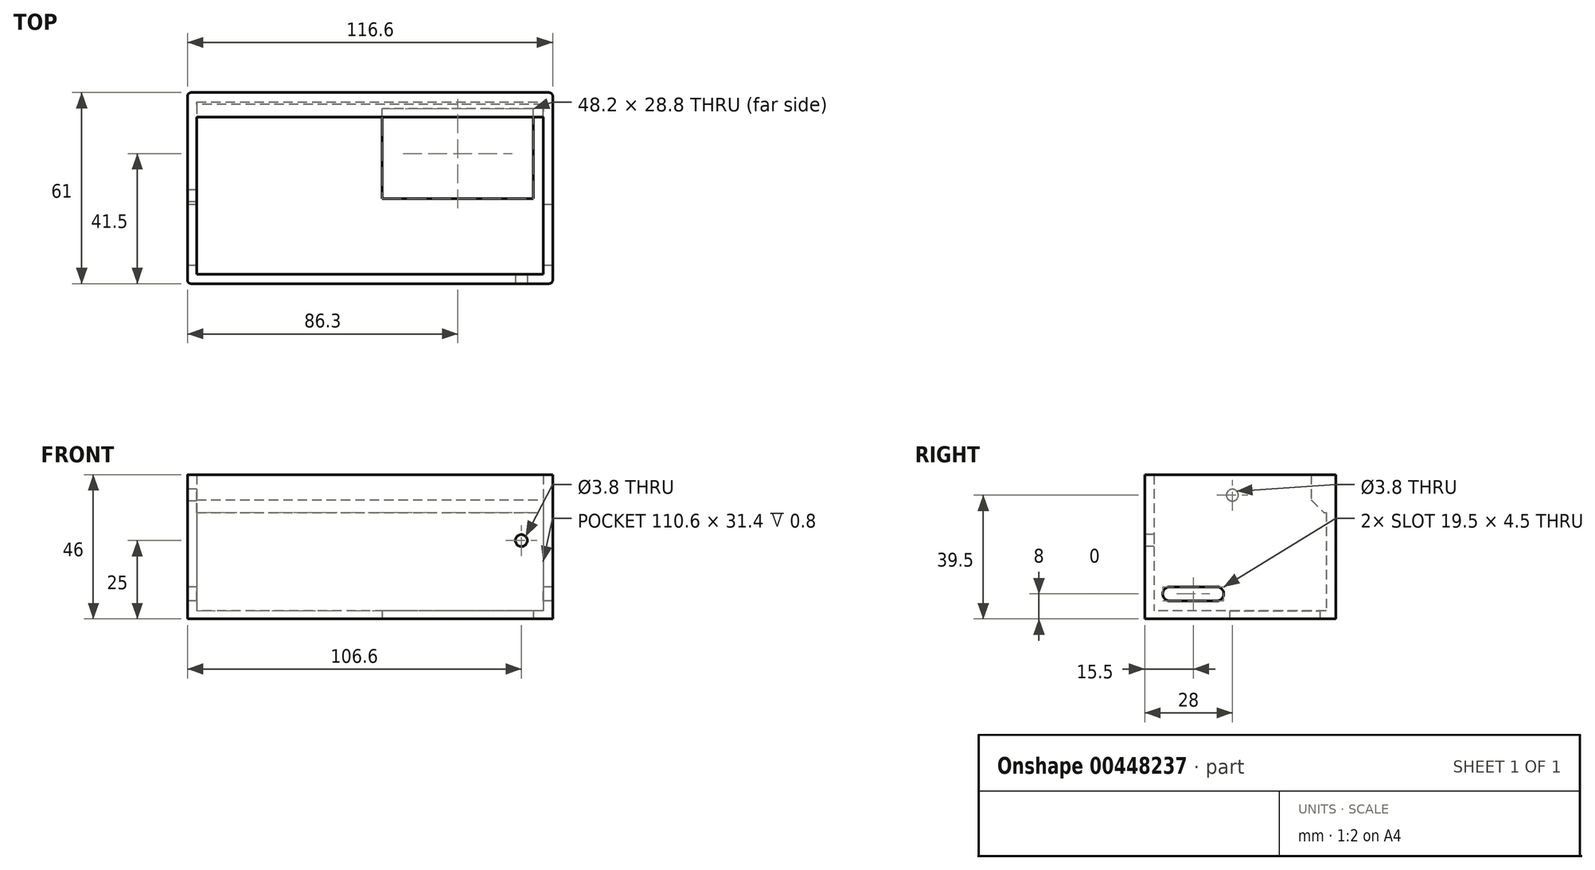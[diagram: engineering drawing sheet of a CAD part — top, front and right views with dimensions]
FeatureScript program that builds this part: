
annotation { "Feature Type Name" : "Feature", "Feature Type Description" : "" }
export const myFeature = defineFeature(function(context is Context, id is Id, definition is map)
    precondition{}
    {
        {
            var Q0;
            Q0=qCreatedBy(makeId("Top.planeOp"),FACE);
            var sketch = newSketch(context, id + "F0", { "sketchPlane" : qUnion([Q0])});
            skLineSegment(sketch, "E0.bottom", {"start": v(55.3, 27.5) * mm, "end": v(-55.3, 27.5) * mm});
            skLineSegment(sketch, "E0.top", {"start": v(55.3, -27.5) * mm, "end": v(-55.3, -27.5) * mm});
            skLineSegment(sketch, "E0.left", {"start": v(55.3, 27.5) * mm, "end": v(55.3, -27.5) * mm});
            skLineSegment(sketch, "E0.right", {"start": v(-55.3, 27.5) * mm, "end": v(-55.3, -27.5) * mm});
            skPoint(sketch, "E0.middle", {"position": v(0, 0) * mm});
            skLineSegment(sketch, "E1.bottom", {"start": v(52.1, -3.4) * mm, "end": v(3.9, -3.4) * mm});
            skLineSegment(sketch, "E1.top", {"start": v(52.1, 25.4) * mm, "end": v(3.9, 25.4) * mm});
            skLineSegment(sketch, "E1.left", {"start": v(52.1, -3.4) * mm, "end": v(52.1, 25.4) * mm});
            skLineSegment(sketch, "E1.right", {"start": v(3.9, -3.4) * mm, "end": v(3.9, 25.4) * mm});
            skPoint(sketch, "E1.middle", {"position": v(28, 11) * mm});
            skSolve(sketch);
        }
        {
            var Q0;
            Q0=makeQuery(id+"F0.imprint","IMPRINT",FACE,{"disambiguationData":[TD([[makeQuery(id+"F0.imprint","IMPRINT",EDGE,{"derivedFrom":sQuery(id+"F0.wireOp",EDGE,"E0.bottom")}),1.0]])]});
            extrude(context, id + "F1", {"entities" : qUnion([Q0]), "depth" : 2.6 * mm, "offsetDistance" : 25 * mm});
        }
        {
            var Q0;
            Q0=qCreatedBy(makeId("Top.planeOp"),FACE);
            var sketch = newSketch(context, id + "F2", { "sketchPlane" : qUnion([Q0])});
            skLineSegment(sketch, "E2.0", {"start": v(-58.3, 30.5) * mm, "end": v(-58.3, -30.5) * mm});
            skLineSegment(sketch, "E2.1", {"start": v(58.3, 30.5) * mm, "end": v(-58.3, 30.5) * mm});
            skLineSegment(sketch, "E2.2", {"start": v(58.3, 30.5) * mm, "end": v(58.3, -30.5) * mm});
            skLineSegment(sketch, "E2.3", {"start": v(58.3, -30.5) * mm, "end": v(-58.3, -30.5) * mm});
            skLineSegment(sketch, "E3.bottom", {"start": v(-55.3, 27.5) * mm, "end": v(55.3, 27.5) * mm});
            skLineSegment(sketch, "E3.top", {"start": v(-55.3, -27.5) * mm, "end": v(55.3, -27.5) * mm});
            skLineSegment(sketch, "E3.left", {"start": v(-55.3, 27.5) * mm, "end": v(-55.3, -27.5) * mm});
            skLineSegment(sketch, "E3.right", {"start": v(55.3, 27.5) * mm, "end": v(55.3, -27.5) * mm});
            skPoint(sketch, "E3.middle", {"position": v(0, 0) * mm});
            skSolve(sketch);
        }
        {
            var Q0;
            Q0=makeQuery(id+"F2.imprint","IMPRINT",FACE,{"disambiguationData":[TD([[makeQuery(id+"F2.imprint","IMPRINT",EDGE,{"derivedFrom":sQuery(id+"F2.wireOp",EDGE,"E2.0")}),1.0]])]});
            extrude(context, id + "F3", {"entities" : qUnion([Q0]), "operationType" : NewBodyOperationType.ADD, "depth" : 46 * mm, "offsetDistance" : 25 * mm});
        }
        {
            var Q0;
            Q0=makeQuery(id+"F3.opExtrude","SWEPT_FACE",FACE,{"disambiguationData":[OSD([sQuery(id+"F2.wireOp",EDGE,"E3.bottom")])]});
            var sketch = newSketch(context, id + "F4", { "sketchPlane" : qUnion([Q0])});
            skLineSegment(sketch, "E4.bottom", {"start": v(-55.3, 46) * mm, "end": v(55.3, 46) * mm});
            skLineSegment(sketch, "E4.top", {"start": v(-55.3, 34) * mm, "end": v(55.3, 34) * mm});
            skLineSegment(sketch, "E4.left", {"start": v(-55.3, 46) * mm, "end": v(-55.3, 34) * mm});
            skLineSegment(sketch, "E4.right", {"start": v(55.3, 46) * mm, "end": v(55.3, 34) * mm});
            skSolve(sketch);
        }
        {
            var Q0;
            Q0=makeQuery(id+"F4.imprint","IMPRINT",FACE,{"disambiguationData":[TD([[makeQuery(id+"F4.imprint","IMPRINT",EDGE,{"derivedFrom":sQuery(id+"F4.wireOp",EDGE,"E4.bottom")}),-1.0]])]});
            extrude(context, id + "F5", {"entities" : qUnion([Q0]), "operationType" : NewBodyOperationType.ADD, "depth" : 4.8 * mm, "offsetDistance" : 25 * mm});
        }
        {
            var Q0;
            Q0=makeQuery(id+"F5.opExtrude","CAP_EDGE",EDGE,{"disambiguationData":[OSD([sQuery(id+"F4.wireOp",EDGE,"E4.top")])],"isStart":false});
            chamfer(context, id + "F6", {"entities" : qUnion([Q0]), "width" : (4) * mm, "tangentPropagation" : true});
        }
        {
            var Q0;
            Q0=makeQuery(id+"F3.opExtrude","SWEPT_FACE",FACE,{"disambiguationData":[OSD([sQuery(id+"F2.wireOp",EDGE,"E2.3")])]});
            var sketch = newSketch(context, id + "F7", { "sketchPlane" : qUnion([Q0])});
            skPoint(sketch, "E5", {"position": v(48.3, 25) * mm});
            skSolve(sketch);
        }
        {
            var Q0;
            Q0=sQuery(id+"F7.wireOp",VERTEX,"E5");
            var Q1;
            Q1=makeQuery(id+"F1.opExtrude","SWEPT_BODY",BODY,{"disambiguationData":[OSD([sQuery(id+"F0.wireOp",EDGE,"E0.bottom"),sQuery(id+"F0.wireOp",EDGE,"E0.top"),sQuery(id+"F0.wireOp",EDGE,"E0.left"),sQuery(id+"F0.wireOp",EDGE,"E0.right"),sQuery(id+"F0.wireOp",EDGE,"E1.bottom"),sQuery(id+"F0.wireOp",EDGE,"E1.top"),sQuery(id+"F0.wireOp",EDGE,"E1.left"),sQuery(id+"F0.wireOp",EDGE,"E1.right")])]});
            hole(context, id + "F8", {"style" : HoleStyle.SIMPLE, "endStyle" : HoleEndStyle.BLIND, "holeDiameter" : 3.8 * mm, "holeDepth" : 15 * mm, "isTappedThrough" : true, "tappedDepth" : 12 * mm, "tapClearance" : 3, "locations" : qUnion([Q0]), "scope" : qUnion([Q1])});
        }
        {
            var Q0;
            Q0=makeQuery(id+"F3.opExtrude","SWEPT_FACE",FACE,{"disambiguationData":[OSD([sQuery(id+"F2.wireOp",EDGE,"E2.0")])]});
            var sketch = newSketch(context, id + "F9", { "sketchPlane" : qUnion([Q0])});
            skPoint(sketch, "E6", {"position": v(2.5, 39.5) * mm});
            skSolve(sketch);
        }
        {
            var Q0;
            Q0=sQuery(id+"F9.wireOp",VERTEX,"E6");
            var Q1;
            Q1=makeQuery(id+"F1.opExtrude","SWEPT_BODY",BODY,{"disambiguationData":[OSD([sQuery(id+"F0.wireOp",EDGE,"E0.bottom"),sQuery(id+"F0.wireOp",EDGE,"E0.top"),sQuery(id+"F0.wireOp",EDGE,"E0.left"),sQuery(id+"F0.wireOp",EDGE,"E0.right"),sQuery(id+"F0.wireOp",EDGE,"E1.bottom"),sQuery(id+"F0.wireOp",EDGE,"E1.top"),sQuery(id+"F0.wireOp",EDGE,"E1.left"),sQuery(id+"F0.wireOp",EDGE,"E1.right")])]});
            hole(context, id + "F10", {"style" : HoleStyle.SIMPLE, "endStyle" : HoleEndStyle.BLIND, "holeDiameter" : 3.8 * mm, "holeDepth" : 15 * mm, "isTappedThrough" : true, "tappedDepth" : 12 * mm, "tapClearance" : 3, "locations" : qUnion([Q0]), "scope" : qUnion([Q1])});
        }
        {
            var Q0;
            {var subQ0=sQuery(id+"F2.wireOp",EDGE,"E2.0");Q0=makeQuery(id+"F9.imprint","IMPRINT",FACE,{"disambiguationData":[TD([[makeQuery(id+"F9.imprint","IMPRINT",EDGE,{"derivedFrom":makeQuery(id+"F3.opExtrude","CAP_EDGE",EDGE,{"disambiguationData":[OSD([subQ0])],"isStart":true})}),1.0]])]});}
            var sketch = newSketch(context, id + "F11", { "sketchPlane" : qUnion([Q0])});
            skLineSegment(sketch, "E7", {"start": v(22.5, 5.75) * mm, "end": v(7.5, 5.75) * mm});
            skLineSegment(sketch, "E8", {"start": v(22.5, 10.25) * mm, "end": v(7.5, 10.25) * mm});
            skArc(sketch, "E9", {"start": v(7.5, 10.25) * mm, "mid": v(5.25, 8) * mm, "end": v(7.5, 5.75) * mm});
            skArc(sketch, "E10", {"start": v(22.5, 5.75) * mm, "mid": v(24.75, 8) * mm, "end": v(22.5, 10.25) * mm});
            skSolve(sketch);
        }
        {
            var Q0;
            Q0=makeQuery(id+"F11.imprint","IMPRINT",FACE,{"disambiguationData":[TD([[makeQuery(id+"F11.imprint","IMPRINT",EDGE,{"derivedFrom":sQuery(id+"F11.wireOp",EDGE,"E7")}),-1.0]])]});
            extrude(context, id + "F12", {"entities" : qUnion([Q0]), "operationType" : NewBodyOperationType.REMOVE, "oppositeDirection" : true, "depth" : 120 * mm, "offsetDistance" : 25 * mm});
        }
        {
            var Q0;
            Q0=makeQuery(id+"F3.opExtrude","SWEPT_EDGE",EDGE,{"disambiguationData":[OSD([sQuery(id+"F2.wireOp",EDGE,"E2.1"),sQuery(id+"F2.wireOp",EDGE,"E2.2")])]});
            var Q1;
            Q1=makeQuery(id+"F3.opExtrude","SWEPT_EDGE",EDGE,{"disambiguationData":[OSD([sQuery(id+"F2.wireOp",EDGE,"E2.2"),sQuery(id+"F2.wireOp",EDGE,"E2.3")])]});
            var Q2;
            Q2=makeQuery(id+"F3.opExtrude","SWEPT_EDGE",EDGE,{"disambiguationData":[OSD([sQuery(id+"F2.wireOp",EDGE,"E2.0"),sQuery(id+"F2.wireOp",EDGE,"E2.3")])]});
            var Q3;
            Q3=makeQuery(id+"F3.opExtrude","SWEPT_EDGE",EDGE,{"disambiguationData":[OSD([sQuery(id+"F2.wireOp",EDGE,"E2.0"),sQuery(id+"F2.wireOp",EDGE,"E2.1")])]});
            fillet(context, id + "F13", {"entities" : qUnion([Q0, Q1, Q2, Q3]), "radius" : 1.2 * mm, "tangentPropagation" : true, "allowEdgeOverflow" : false});
        }
    });
